# Revit family: PRD_FrankeWS_WCFlshngVlvs_FlushingPlate_AQUA555,557
name_source: partatom
category: Plumbing Fixtures
revit_build: Autodesk Revit 2018 (Build: 20190510_1515(x64)
units: mm (PartAtom-declared; Revit-internal decimal feet)

## family parameters
Cut with Voids When Loaded = No
Host = Face
OmniClass Number = 23.45.05.14.99
OmniClass Title = Other Sanitary Washing Plumbing Fixtures
Part Type = Normal
Room Calculation Point = No
Round Connector Dimension = Use Diameter
Shared = No

## types (2) — shared parameters
AssetType = Fixed
Category = Pr_40_20_93_91, WC flushing valves
Color = Stainless steel
Default Elevation = 1000 mm  [stored 3.28084 ft]
DurationUnit = year
FlushValveMaterial = PRD_AR_StainlessSteel_SatinFinished
FlushingRate = 0.0 L/s
GrossWeight = 0.55 kg
HasIntegralShutOffDevice = No
IfcExportAs = IfcValveType
IfcExportType = FLUSHING
IsHighPressure = No
Manufacturer = KWC Group AG
ManufacturerName = KWC Group AG
ManufacturerURL = www.kwc.com
Material = Stainless steel
NBSDescription = WC flushing valves
NBSReference = 45-35-70/389
NetWeight = 0.52 kg
NominalHeight = 22 mm  [stored 0.0721785 ft]
NominalLength = 148 mm  [stored 0.485564 ft]
NominalWidth = 207 mm  [stored 0.679134 ft]
ProductInformation = https://pim.kwc.com
Size = 207 x 148 x 22 mm
URL = www.kwc.com
Uniclass2015Code = Pr_40_20_93_91
Uniclass2015Title = WC flushing valves
Uniclass2015Version = Products v1.10
Version = 1
WarrantyDurationUnit = year

## per-type parameters (varying)
| type | AQUA555 | AQUA557 | BIMObjectName | Description | Finish | ModelNumber | Name |
| AQUA555 | Yes | No | PRD_AR_WCFlushingValves_FlushingPlate_AQUA555 | Flushing plate for wall-installation cistern, operation from front, 2-level flushing or start/stop flushing, consisting of operating button, button mounting, installation frame, fixing bolts and securing screw, dimensions 207 x 148 mm (W x H). made of stainless steel | Satin finished | 2000067493 | Flushing plate AQUA555 |
| AQUA557 | No | Yes | PRD_AR_WCFlushingValves_FlushingPlate_AQUA557 | Flushing plate for wall-installation cistern, operation from front, consisting of operating button, button mounting, installation frame, fixing bolts and securing screw, made of stainless steel. Dimensions 207 x 148 mm (B x H). |  | 2000067429 | Flushing plate AQUA557 |

note: column(s) folded — value = type name in every type: Model, ModelReference

note: [stored X ft] marks values corroborated as IEEE doubles in the binary element streams (Revit-internal decimal feet)

## geometry (parser evidence)
native form markers: Sweep x2
no freeform markers — native parametric forms only
